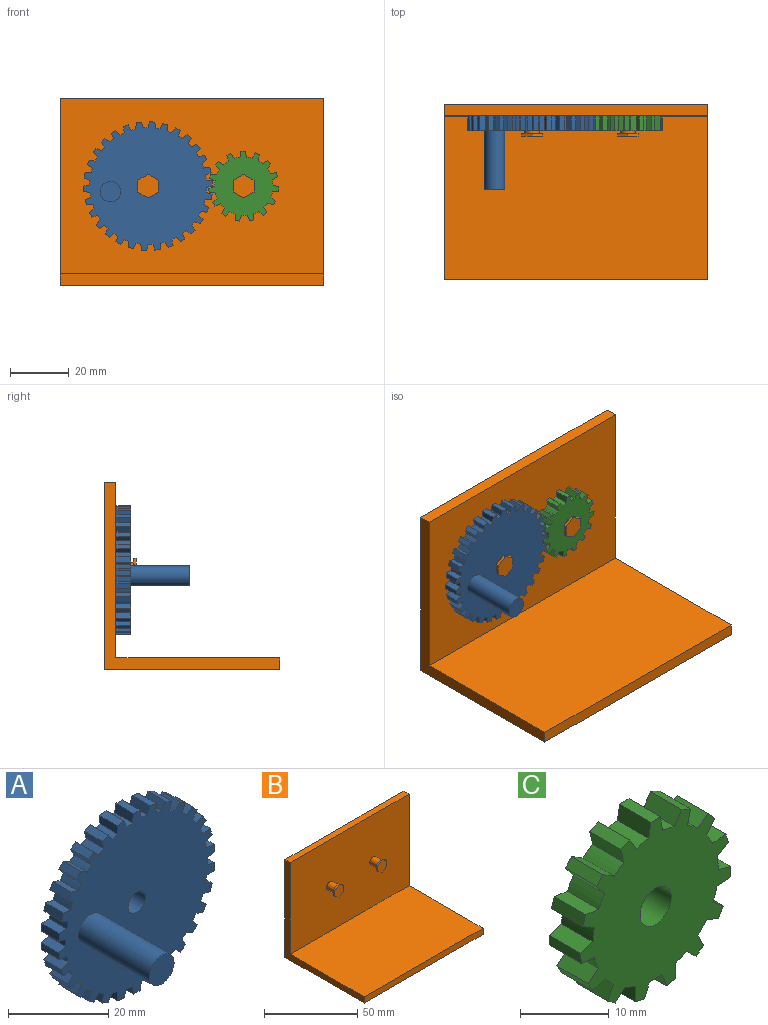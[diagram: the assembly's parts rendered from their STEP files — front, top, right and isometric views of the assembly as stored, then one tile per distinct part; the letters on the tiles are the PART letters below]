
ASSEMBLY  parts=3 mates=2
PART A: 125 faces, bbox 43.9x25x44 mm
  f0: cylinder r=20mm len=5mm, axis (0,1,0), area 8.3mm2, adj f33,f34,f82,f85
  f1: cylinder r=20mm len=5mm, axis (0,1,0), area 8.3mm2, adj f33,f34,f84,f88
  f2: cylinder r=20mm len=5mm, axis (0,1,0), area 8.3mm2, adj f33,f34,f87,f91
  f3: cylinder r=20mm len=5mm, axis (0,1,0), area 8.3mm2, adj f33,f34,f90,f94
  f4: cylinder r=20mm len=5mm, axis (0,1,0), area 8.3mm2, adj f33,f34,f93,f97
  f5: cylinder r=20mm len=5mm, axis (0,1,0), area 8.3mm2, adj f33,f34,f96,f100
  f6: cylinder r=20mm len=5mm, axis (0,1,0), area 8.3mm2, adj f33,f34,f99,f103
  f7: cylinder r=20mm len=5mm, axis (0,1,0), area 8.3mm2, adj f33,f34,f102,f106
  f8: cylinder r=20mm len=5mm, axis (0,1,0), area 8.3mm2, adj f33,f34,f105,f109
  f9: cylinder r=20mm len=5mm, axis (0,1,0), area 8.3mm2, adj f33,f34,f108,f112
  f10: cylinder r=20mm len=5mm, axis (0,1,0), area 8.3mm2, adj f33,f34,f111,f115
  f11: cylinder r=20mm len=5mm, axis (0,1,0), area 8.3mm2, adj f33,f34,f114,f118
  f12: cylinder r=20mm len=5mm, axis (0,1,0), area 8.3mm2, adj f33,f34,f117,f121
  f13: cylinder r=20mm len=5mm, axis (0,1,0), area 8.3mm2, adj f33,f34,f37,f119
  f14: cylinder r=20mm len=5mm, axis (0,1,0), area 8.3mm2, adj f33,f34,f36,f40
  f15: cylinder r=20mm len=5mm, axis (0,1,0), area 8.3mm2, adj f33,f34,f39,f43
  f16: cylinder r=20mm len=5mm, axis (0,1,0), area 8.3mm2, adj f33,f34,f42,f46
  f17: cylinder r=20mm len=5mm, axis (0,1,0), area 8.3mm2, adj f33,f34,f45,f49
  f18: cylinder r=20mm len=5mm, axis (0,1,0), area 8.3mm2, adj f33,f34,f48,f52
  f19: cylinder r=20mm len=5mm, axis (0,1,0), area 8.3mm2, adj f33,f34,f51,f55
  f20: cylinder r=20mm len=5mm, axis (0,1,0), area 8.3mm2, adj f33,f34,f54,f58
  f21: cylinder r=20mm len=5mm, axis (0,1,0), area 8.3mm2, adj f33,f34,f57,f61
  f22: cylinder r=20mm len=5mm, axis (0,1,0), area 8.3mm2, adj f33,f34,f60,f64
  f23: cylinder r=20mm len=5mm, axis (0,1,0), area 8.3mm2, adj f33,f34,f63,f67
  f24: cylinder r=20mm len=5mm, axis (0,1,0), area 8.3mm2, adj f33,f34,f66,f70
  f25: cylinder r=20mm len=5mm, axis (0,1,0), area 8.3mm2, adj f33,f34,f69,f73
  f26: cylinder r=20mm len=5mm, axis (0,1,0), area 8.3mm2, adj f33,f34,f72,f76
  f27: cylinder r=20mm len=5mm, axis (0,1,0), area 8.3mm2, adj f33,f34,f75,f79
  f28: cylinder r=20mm len=5mm, axis (0,1,0), area 8.3mm2, adj f32,f33,f34,f78
  f29: cylinder r=20mm len=5mm, axis (0,1,0), area 8.3mm2, adj f30,f33,f34,f81
  f30: plane 5x2.04mm, normal (0.98,0,0.17), area 10.4mm2, adj f29,f31,f33,f34
  f31: plane 5x1.8mm, normal (0,0,1), area 9mm2, adj f30,f32,f33,f34
  f32: plane 5x2.04mm, normal (-0.98,0,0.17), area 10.4mm2, adj f28,f31,f33,f34
  f33: plane 44x43.95mm, normal (0,-1,0), area 1328.7mm2, adj f0,f1,f2,f3,f4,f5,f6,f7
  f34: plane 44x43.95mm, normal (0,1,0), area 1367.2mm2, adj f0,f1,f2,f3,f4,f5,f6,f7
  f35: plane 5x1.8mm, normal (0,0,-1), area 9mm2, adj f33,f34,f36,f37
  f36: plane 5x2.04mm, normal (-0.98,0,-0.17), area 10.4mm2, adj f14,f33,f34,f35
  f37: plane 5x2.04mm, normal (0.98,0,-0.17), area 10.4mm2, adj f13,f33,f34,f35
  f38: plane 5x1.76mm, normal (-0.21,0,-0.98), area 9mm2, adj f33,f34,f39,f40
  f39: plane 5x2.07mm, normal (-1,0,0.03), area 10.4mm2, adj f15,f33,f34,f38
  f40: plane 5x1.92mm, normal (0.93,0,-0.37), area 10.4mm2, adj f14,f33,f34,f38
  f41: plane 5x1.64mm, normal (-0.41,0,-0.91), area 9mm2, adj f33,f34,f42,f43
  f42: plane 5x2.01mm, normal (-0.97,0,0.24), area 10.4mm2, adj f16,f33,f34,f41
  f43: plane 5x1.72mm, normal (0.83,0,-0.56), area 10.4mm2, adj f15,f33,f34,f41
  f44: plane 5x1.46mm, normal (-0.59,0,-0.81), area 9mm2, adj f33,f34,f45,f46
  f45: plane 5x1.86mm, normal (-0.9,0,0.44), area 10.4mm2, adj f17,f33,f34,f44
  f46: plane 5x1.49mm, normal (0.69,0,-0.72), area 10.4mm2, adj f16,f33,f34,f44
  f47: plane 5x1.34mm, normal (-0.74,0,-0.67), area 9mm2, adj f33,f34,f48,f49
  f48: plane 5x1.63mm, normal (-0.79,0,0.62), area 10.4mm2, adj f18,f33,f34,f47
  f49: plane 5x1.76mm, normal (0.53,0,-0.85), area 10.4mm2, adj f17,f33,f34,f47
  f50: plane 5x1.56mm, normal (-0.87,0,-0.5), area 9mm2, adj f33,f34,f51,f52
  f51: plane 5x1.59mm, normal (-0.64,0,0.77), area 10.4mm2, adj f19,f33,f34,f50
  f52: plane 5x1.95mm, normal (0.34,0,-0.94), area 10.4mm2, adj f18,f33,f34,f50
  f53: plane 5x1.71mm, normal (-0.95,0,-0.31), area 9mm2, adj f33,f34,f54,f55
  f54: plane 5x1.83mm, normal (-0.47,0,0.88), area 10.4mm2, adj f20,f33,f34,f53
  f55: plane 5x2.05mm, normal (0.14,0,-0.99), area 10.4mm2, adj f19,f33,f34,f53
  f56: plane 5x1.79mm, normal (-0.99,0,-0.1), area 9mm2, adj f33,f34,f57,f58
  f57: plane 5x1.99mm, normal (-0.28,0,0.96), area 10.4mm2, adj f21,f33,f34,f56
  f58: plane 5x2.07mm, normal (-0.07,0,-1), area 10.4mm2, adj f20,f33,f34,f56
  f59: plane 5x1.79mm, normal (-0.99,0,0.1), area 9mm2, adj f33,f34,f60,f61
  f60: plane 5x2.07mm, normal (-0.07,0,1), area 10.4mm2, adj f22,f33,f34,f59
  f61: plane 5x1.99mm, normal (-0.28,0,-0.96), area 10.4mm2, adj f21,f33,f34,f59
  f62: plane 5x1.71mm, normal (-0.95,0,0.31), area 9mm2, adj f33,f34,f63,f64
  f63: plane 5x2.05mm, normal (0.14,0,0.99), area 10.4mm2, adj f23,f33,f34,f62
  f64: plane 5x1.83mm, normal (-0.47,0,-0.88), area 10.4mm2, adj f22,f33,f34,f62
  f65: plane 5x1.56mm, normal (-0.87,0,0.5), area 9mm2, adj f33,f34,f66,f67
  f66: plane 5x1.95mm, normal (0.34,0,0.94), area 10.4mm2, adj f24,f33,f34,f65
  f67: plane 5x1.59mm, normal (-0.64,0,-0.77), area 10.4mm2, adj f23,f33,f34,f65
  f68: plane 5x1.34mm, normal (-0.74,0,0.67), area 9mm2, adj f33,f34,f69,f70
  f69: plane 5x1.76mm, normal (0.53,0,0.85), area 10.4mm2, adj f25,f33,f34,f68
  f70: plane 5x1.63mm, normal (-0.79,0,-0.62), area 10.4mm2, adj f24,f33,f34,f68
  f71: plane 5x1.46mm, normal (-0.59,0,0.81), area 9mm2, adj f33,f34,f72,f73
  f72: plane 5x1.49mm, normal (0.69,0,0.72), area 10.4mm2, adj f26,f33,f34,f71
  f73: plane 5x1.86mm, normal (-0.9,0,-0.44), area 10.4mm2, adj f25,f33,f34,f71
  f74: plane 5x1.64mm, normal (-0.41,0,0.91), area 9mm2, adj f33,f34,f75,f76
  f75: plane 5x1.72mm, normal (0.83,0,0.56), area 10.4mm2, adj f27,f33,f34,f74
  f76: plane 5x2.01mm, normal (-0.97,0,-0.24), area 10.4mm2, adj f26,f33,f34,f74
  f77: plane 5x1.76mm, normal (-0.21,0,0.98), area 9mm2, adj f33,f34,f78,f79
  f78: plane 5x1.92mm, normal (0.93,0,0.37), area 10.4mm2, adj f28,f33,f34,f77
  f79: plane 5x2.07mm, normal (-1,0,-0.03), area 10.4mm2, adj f27,f33,f34,f77
  f80: plane 5x1.76mm, normal (0.21,0,0.98), area 9mm2, adj f33,f34,f81,f82
  f81: plane 5x1.92mm, normal (-0.93,0,0.37), area 10.4mm2, adj f29,f33,f34,f80
  f82: plane 5x2.07mm, normal (1,0,-0.03), area 10.4mm2, adj f0,f33,f34,f80
  f83: plane 5x1.64mm, normal (0.41,0,0.91), area 9mm2, adj f33,f34,f84,f85
  f84: plane 5x2.01mm, normal (0.97,0,-0.24), area 10.4mm2, adj f1,f33,f34,f83
  f85: plane 5x1.72mm, normal (-0.83,0,0.56), area 10.4mm2, adj f0,f33,f34,f83
  f86: plane 5x1.46mm, normal (0.59,0,0.81), area 9mm2, adj f33,f34,f87,f88
  f87: plane 5x1.86mm, normal (0.9,0,-0.44), area 10.4mm2, adj f2,f33,f34,f86
  f88: plane 5x1.49mm, normal (-0.69,0,0.72), area 10.4mm2, adj f1,f33,f34,f86
  f89: plane 5x1.34mm, normal (0.74,0,0.67), area 9mm2, adj f33,f34,f90,f91
  f90: plane 5x1.63mm, normal (0.79,0,-0.62), area 10.4mm2, adj f3,f33,f34,f89
  f91: plane 5x1.76mm, normal (-0.53,0,0.85), area 10.4mm2, adj f2,f33,f34,f89
  f92: plane 5x1.56mm, normal (0.87,0,0.5), area 9mm2, adj f33,f34,f93,f94
  f93: plane 5x1.59mm, normal (0.64,0,-0.77), area 10.4mm2, adj f4,f33,f34,f92
  f94: plane 5x1.95mm, normal (-0.34,0,0.94), area 10.4mm2, adj f3,f33,f34,f92
  f95: plane 5x1.71mm, normal (0.95,0,0.31), area 9mm2, adj f33,f34,f96,f97
  f96: plane 5x1.83mm, normal (0.47,0,-0.88), area 10.4mm2, adj f5,f33,f34,f95
  f97: plane 5x2.05mm, normal (-0.14,0,0.99), area 10.4mm2, adj f4,f33,f34,f95
  f98: plane 5x1.79mm, normal (0.99,0,0.1), area 9mm2, adj f33,f34,f99,f100
  f99: plane 5x1.99mm, normal (0.28,0,-0.96), area 10.4mm2, adj f6,f33,f34,f98
  f100: plane 5x2.07mm, normal (0.07,0,1), area 10.4mm2, adj f5,f33,f34,f98
  f101: plane 5x1.79mm, normal (0.99,0,-0.1), area 9mm2, adj f33,f34,f102,f103
  f102: plane 5x2.07mm, normal (0.07,0,-1), area 10.4mm2, adj f7,f33,f34,f101
  f103: plane 5x1.99mm, normal (0.28,0,0.96), area 10.4mm2, adj f6,f33,f34,f101
  f104: plane 5x1.71mm, normal (0.95,0,-0.31), area 9mm2, adj f33,f34,f105,f106
  f105: plane 5x2.05mm, normal (-0.14,0,-0.99), area 10.4mm2, adj f8,f33,f34,f104
  f106: plane 5x1.83mm, normal (0.47,0,0.88), area 10.4mm2, adj f7,f33,f34,f104
  f107: plane 5x1.56mm, normal (0.87,0,-0.5), area 9mm2, adj f33,f34,f108,f109
  f108: plane 5x1.95mm, normal (-0.34,0,-0.94), area 10.4mm2, adj f9,f33,f34,f107
  f109: plane 5x1.59mm, normal (0.64,0,0.77), area 10.4mm2, adj f8,f33,f34,f107
  f110: plane 5x1.34mm, normal (0.74,0,-0.67), area 9mm2, adj f33,f34,f111,f112
  f111: plane 5x1.76mm, normal (-0.53,0,-0.85), area 10.4mm2, adj f10,f33,f34,f110
  f112: plane 5x1.63mm, normal (0.79,0,0.62), area 10.4mm2, adj f9,f33,f34,f110
  f113: plane 5x1.46mm, normal (0.59,0,-0.81), area 9mm2, adj f33,f34,f114,f115
  f114: plane 5x1.49mm, normal (-0.69,0,-0.72), area 10.4mm2, adj f11,f33,f34,f113
  f115: plane 5x1.86mm, normal (0.9,0,0.44), area 10.4mm2, adj f10,f33,f34,f113
  f116: plane 5x1.64mm, normal (0.41,0,-0.91), area 9mm2, adj f33,f34,f117,f118
  f117: plane 5x1.72mm, normal (-0.83,0,-0.56), area 10.4mm2, adj f12,f33,f34,f116
  f118: plane 5x2.01mm, normal (0.97,0,0.24), area 10.4mm2, adj f11,f33,f34,f116
  f119: plane 5x1.92mm, normal (-0.93,0,-0.37), area 10.4mm2, adj f13,f33,f34,f120
  f120: plane 5x1.76mm, normal (0.21,0,-0.98), area 9mm2, adj f33,f34,f119,f121
  f121: plane 5x2.07mm, normal (1,0,0.03), area 10.4mm2, adj f12,f33,f34,f120
  f122: cylinder r=2.5mm len=5mm, axis (0,-1,0), area 78.5mm2, adj f33,f34
  f123: cylinder r=3.5mm len=20mm, axis (0,1,0), area 439.8mm2, adj f33,f124
  f124: plane 7x7mm, normal (0,-1,0), area 38.5mm2, adj f123
PART B: 26 faces, bbox 90x60x64 mm
  f0: plane 90x64mm, normal (0,1,0), area 5760mm2, adj f1,f3,f5,f7
  f1: plane 64x60mm, normal (-1,0,0), area 480mm2, adj f0,f2,f4,f5,f6,f7
  f2: plane 90x4mm, normal (0,-1,0), area 360mm2, adj f1,f3,f4,f5
  f3: plane 64x60mm, normal (1,0,0), area 480mm2, adj f0,f2,f4,f5,f6,f7
  f4: plane 90x56mm, normal (0,0,1), area 5040mm2, adj f1,f2,f3,f6
  f5: plane 90x60mm, normal (0,0,-1), area 5400mm2, adj f0,f1,f2,f3
  f6: plane 90x60mm, normal (0,-1,0), area 5360.7mm2, adj f1,f3,f4,f7,f8,f9
  f7: plane 90x4mm, normal (0,0,1), area 360mm2, adj f0,f1,f3,f6
  f8: cylinder r=2.5mm len=6mm, axis (0,1,0), area 94.2mm2, adj f6,f17
  f9: cylinder r=2.5mm len=6mm, axis (0,1,0), area 94.2mm2, adj f6,f25
  f10: plane 3.5x2.02mm, normal (-0.5,0,0.87), area 4mm2, adj f11,f15,f16,f17
  f11: plane 4.04x1mm, normal (-1,0,0), area 4mm2, adj f10,f12,f16,f17
  f12: plane 3.5x2.02mm, normal (-0.5,0,-0.87), area 4mm2, adj f11,f13,f16,f17
  f13: plane 3.5x2.02mm, normal (0.5,0,-0.87), area 4mm2, adj f12,f14,f16,f17
  f14: plane 4.04x1mm, normal (1,0,0), area 4mm2, adj f13,f15,f16,f17
  f15: plane 3.5x2.02mm, normal (0.5,0,0.87), area 4mm2, adj f10,f14,f16,f17
  f16: plane 8.08x7mm, normal (0,-1,0), area 42.4mm2, adj f10,f11,f12,f13,f14,f15
  f17: plane 8.08x7mm, normal (0,1,0), area 22.8mm2, adj f8,f10,f11,f12,f13,f14,f15
  f18: plane 3.5x2.02mm, normal (0.5,0,-0.87), area 4mm2, adj f19,f23,f24,f25
  f19: plane 4.04x1mm, normal (1,0,0), area 4mm2, adj f18,f20,f24,f25
  f20: plane 3.5x2.02mm, normal (0.5,0,0.87), area 4mm2, adj f19,f21,f24,f25
  f21: plane 3.5x2.02mm, normal (-0.5,0,0.87), area 4mm2, adj f20,f22,f24,f25
  f22: plane 4.04x1mm, normal (-1,0,0), area 4mm2, adj f21,f23,f24,f25
  f23: plane 3.5x2.02mm, normal (-0.5,0,-0.87), area 4mm2, adj f18,f22,f24,f25
  f24: plane 8.08x7mm, normal (0,-1,0), area 42.4mm2, adj f18,f19,f20,f21,f22,f23
  f25: plane 8.08x7mm, normal (0,1,0), area 22.8mm2, adj f9,f18,f19,f20,f21,f22,f23
PART C: 63 faces, bbox 24x5x23.9 mm
  f0: cylinder r=10mm len=5mm, axis (0,1,0), area 9.8mm2, adj f18,f19,f43,f46
  f1: cylinder r=10mm len=5mm, axis (0,1,0), area 9.8mm2, adj f18,f19,f45,f49
  f2: cylinder r=10mm len=5mm, axis (0,1,0), area 9.8mm2, adj f18,f19,f48,f52
  f3: cylinder r=10mm len=5mm, axis (0,1,0), area 9.8mm2, adj f18,f19,f51,f55
  f4: cylinder r=10mm len=5mm, axis (0,1,0), area 9.8mm2, adj f18,f19,f54,f58
  f5: cylinder r=10mm len=5mm, axis (0,1,0), area 9.8mm2, adj f18,f19,f57,f61
  f6: cylinder r=10mm len=5mm, axis (0,1,0), area 9.8mm2, adj f18,f19,f22,f59
  f7: cylinder r=10mm len=5mm, axis (0,1,0), area 9.8mm2, adj f18,f19,f21,f25
  f8: cylinder r=10mm len=5mm, axis (0,1,0), area 9.8mm2, adj f18,f19,f24,f28
  f9: cylinder r=10mm len=5mm, axis (0,1,0), area 9.8mm2, adj f18,f19,f27,f31
  f10: cylinder r=10mm len=5mm, axis (0,1,0), area 9.8mm2, adj f18,f19,f30,f34
  f11: cylinder r=10mm len=5mm, axis (0,1,0), area 9.8mm2, adj f18,f19,f33,f37
  f12: cylinder r=10mm len=5mm, axis (0,1,0), area 9.8mm2, adj f18,f19,f36,f40
  f13: cylinder r=10mm len=5mm, axis (0,1,0), area 9.8mm2, adj f17,f18,f19,f39
  f14: cylinder r=10mm len=5mm, axis (0,1,0), area 9.8mm2, adj f15,f18,f19,f42
  f15: plane 5x2.06mm, normal (0.98,0,0.17), area 10.5mm2, adj f14,f16,f18,f19
  f16: plane 5x1.5mm, normal (0,0,1), area 7.5mm2, adj f15,f17,f18,f19
  f17: plane 5x2.06mm, normal (-0.98,0,0.17), area 10.5mm2, adj f13,f16,f18,f19
  f18: plane 24.03x23.89mm, normal (0,-1,0), area 350.8mm2, adj f0,f1,f2,f3,f4,f5,f6,f7
  f19: plane 24.03x23.89mm, normal (0,1,0), area 350.8mm2, adj f0,f1,f2,f3,f4,f5,f6,f7
  f20: plane 5x1.47mm, normal (-0.21,0,-0.98), area 7.5mm2, adj f18,f19,f21,f22
  f21: plane 5x2.09mm, normal (-1,0,0.03), area 10.5mm2, adj f7,f18,f19,f20
  f22: plane 5x1.94mm, normal (0.93,0,-0.37), area 10.5mm2, adj f6,f18,f19,f20
  f23: plane 5x1.21mm, normal (-0.59,0,-0.81), area 7.5mm2, adj f18,f19,f24,f25
  f24: plane 5x1.88mm, normal (-0.9,0,0.44), area 10.5mm2, adj f8,f18,f19,f23
  f25: plane 5x1.51mm, normal (0.69,0,-0.72), area 10.5mm2, adj f7,f18,f19,f23
  f26: plane 5x1.3mm, normal (-0.87,0,-0.5), area 7.5mm2, adj f18,f19,f27,f28
  f27: plane 5x1.6mm, normal (-0.64,0,0.77), area 10.5mm2, adj f9,f18,f19,f26
  f28: plane 5x1.97mm, normal (0.34,0,-0.94), area 10.5mm2, adj f8,f18,f19,f26
  f29: plane 5x1.49mm, normal (-0.99,0,-0.1), area 7.5mm2, adj f18,f19,f30,f31
  f30: plane 5x2.01mm, normal (-0.28,0,0.96), area 10.5mm2, adj f10,f18,f19,f29
  f31: plane 5x2.09mm, normal (-0.07,0,-1), area 10.5mm2, adj f9,f18,f19,f29
  f32: plane 5x1.43mm, normal (-0.95,0,0.31), area 7.5mm2, adj f18,f19,f33,f34
  f33: plane 5x2.07mm, normal (0.14,0,0.99), area 10.5mm2, adj f11,f18,f19,f32
  f34: plane 5x1.85mm, normal (-0.47,0,-0.88), area 10.5mm2, adj f10,f18,f19,f32
  f35: plane 5x1.11mm, normal (-0.74,0,0.67), area 7.5mm2, adj f18,f19,f36,f37
  f36: plane 5x1.78mm, normal (0.53,0,0.85), area 10.5mm2, adj f12,f18,f19,f35
  f37: plane 5x1.65mm, normal (-0.79,0,-0.62), area 10.5mm2, adj f11,f18,f19,f35
  f38: plane 5x1.37mm, normal (-0.41,0,0.91), area 7.5mm2, adj f18,f19,f39,f40
  f39: plane 5x1.74mm, normal (0.83,0,0.56), area 10.5mm2, adj f13,f18,f19,f38
  f40: plane 5x2.03mm, normal (-0.97,0,-0.24), area 10.5mm2, adj f12,f18,f19,f38
  f41: plane 5x1.37mm, normal (0.41,0,0.91), area 7.5mm2, adj f18,f19,f42,f43
  f42: plane 5x1.74mm, normal (-0.83,0,0.56), area 10.5mm2, adj f14,f18,f19,f41
  f43: plane 5x2.03mm, normal (0.97,0,-0.24), area 10.5mm2, adj f0,f18,f19,f41
  f44: plane 5x1.11mm, normal (0.74,0,0.67), area 7.5mm2, adj f18,f19,f45,f46
  f45: plane 5x1.65mm, normal (0.79,0,-0.62), area 10.5mm2, adj f1,f18,f19,f44
  f46: plane 5x1.78mm, normal (-0.53,0,0.85), area 10.5mm2, adj f0,f18,f19,f44
  f47: plane 5x1.43mm, normal (0.95,0,0.31), area 7.5mm2, adj f18,f19,f48,f49
  f48: plane 5x1.85mm, normal (0.47,0,-0.88), area 10.5mm2, adj f2,f18,f19,f47
  f49: plane 5x2.07mm, normal (-0.14,0,0.99), area 10.5mm2, adj f1,f18,f19,f47
  f50: plane 5x1.49mm, normal (0.99,0,-0.1), area 7.5mm2, adj f18,f19,f51,f52
  f51: plane 5x2.09mm, normal (0.07,0,-1), area 10.5mm2, adj f3,f18,f19,f50
  f52: plane 5x2.01mm, normal (0.28,0,0.96), area 10.5mm2, adj f2,f18,f19,f50
  f53: plane 5x1.3mm, normal (0.87,0,-0.5), area 7.5mm2, adj f18,f19,f54,f55
  f54: plane 5x1.97mm, normal (-0.34,0,-0.94), area 10.5mm2, adj f4,f18,f19,f53
  f55: plane 5x1.6mm, normal (0.64,0,0.77), area 10.5mm2, adj f3,f18,f19,f53
  f56: plane 5x1.21mm, normal (0.59,0,-0.81), area 7.5mm2, adj f18,f19,f57,f58
  f57: plane 5x1.51mm, normal (-0.69,0,-0.72), area 10.5mm2, adj f5,f18,f19,f56
  f58: plane 5x1.88mm, normal (0.9,0,0.44), area 10.5mm2, adj f4,f18,f19,f56
  f59: plane 5x1.94mm, normal (-0.93,0,-0.37), area 10.5mm2, adj f6,f18,f19,f60
  f60: plane 5x1.47mm, normal (0.21,0,-0.98), area 7.5mm2, adj f18,f19,f59,f61
  f61: plane 5x2.09mm, normal (1,0,0.03), area 10.5mm2, adj f5,f18,f19,f60
  f62: cylinder r=2.5mm len=5mm, axis (0,-1,0), area 78.5mm2, adj f18,f19
PLACE A rot(axis=(0,-1,0),8.4deg) t=(-27.1,34.51,25.26)mm
PLACE B t=(-12.1,8.51,-8.74)mm fixed
PLACE C rot(axis=(0,-1,0),73.2deg) t=(5.6,34.51,25.26)mm
MATE revolute B.f9 <-> C.f62  axis (0,-1,0) through (5.6,34.51,25.26)mm
MATE revolute B.f8 <-> A.f0  axis (0,-1,0) through (-27.1,34.51,25.26)mm
